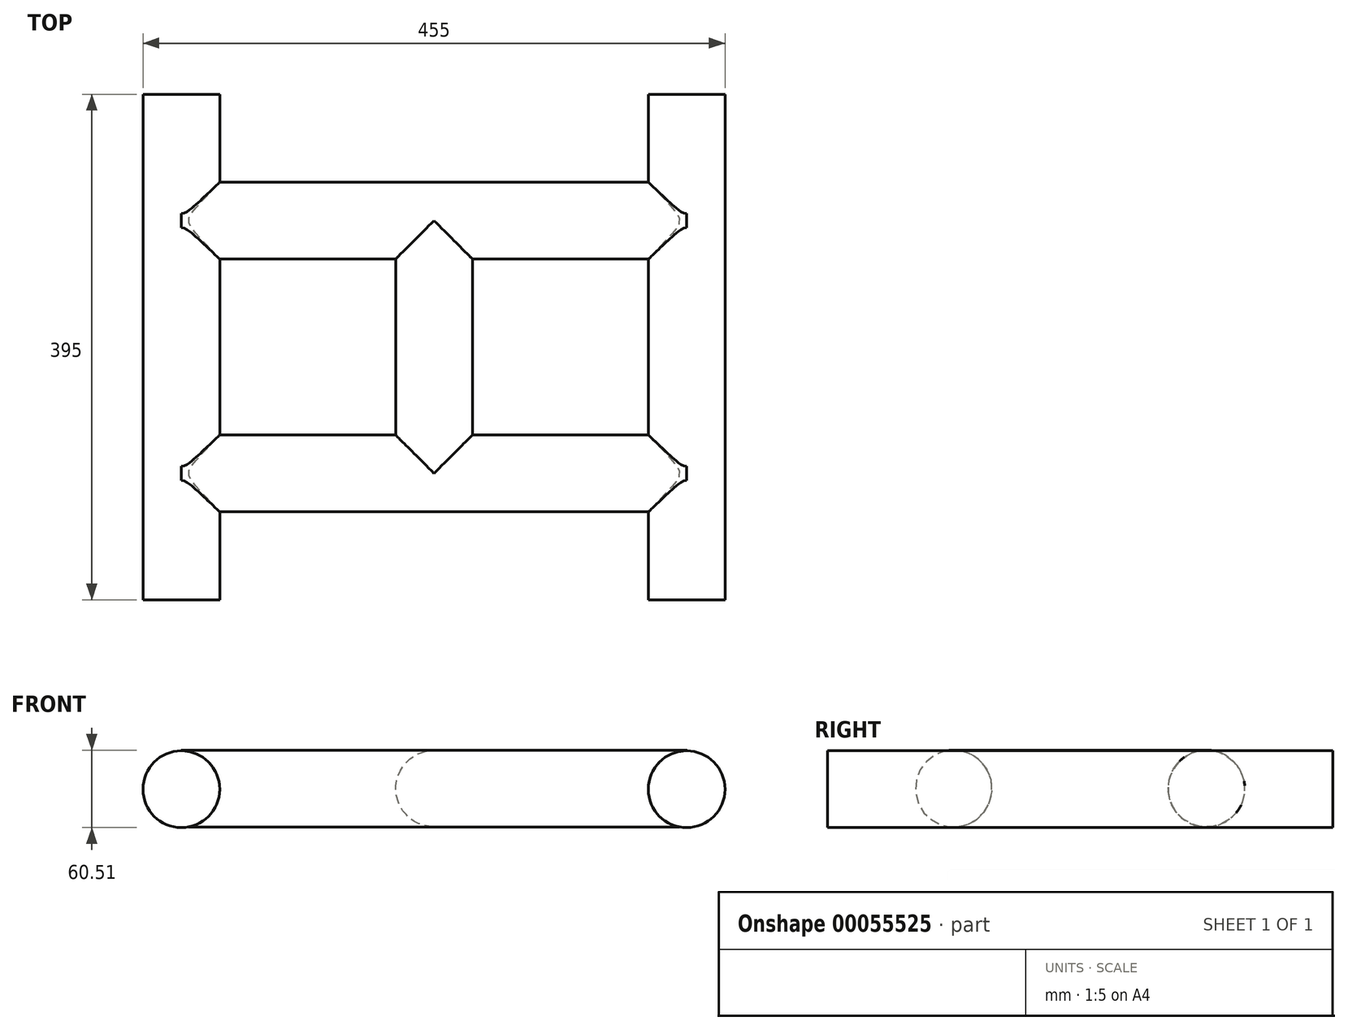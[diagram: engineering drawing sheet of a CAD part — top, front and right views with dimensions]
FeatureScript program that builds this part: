
annotation { "Feature Type Name" : "Feature", "Feature Type Description" : "" }
export const myFeature = defineFeature(function(context is Context, id is Id, definition is map)
    precondition{}
    {
        {
            var Q0;
            Q0=qCreatedBy(makeId("Front.planeOp"),FACE);
            var sketch = newSketch(context, id + "F0", { "sketchPlane" : qUnion([Q0])});
            skCircle(sketch, "E0", {"center": v(0, 0) * mm, "radius": 30 * mm});
            skCircle(sketch, "E1", {"center": v(-197.5, -0.5) * mm, "radius": 30 * mm});
            skSolve(sketch);
        }
        {
            var Q0;
            Q0=makeQuery(id+"F0.imprint","IMPRINT",FACE,{"disambiguationData":[TD([[makeQuery(id+"F0.imprint","IMPRINT",EDGE,{"derivedFrom":sQuery(id+"F0.wireOp",EDGE,"E1")}),1.0]])]});
            extrude(context, id + "F1", {"entities" : qUnion([Q0]), "endBound" : BoundingType.SYMMETRIC, "depth" : 395 * mm});
        }
        {
            var Q0;
            Q0 = qSketchRegion(id + "F0", true);
            extrude(context, id + "F2", {"entities" : qUnion([Q0]), "operationType" : NewBodyOperationType.ADD, "endBound" : BoundingType.SYMMETRIC, "depth" : 395 / 2 * mm});
        }
        {
            var Q0;
            Q0=makeQuery(id+"F2.opExtrude","SWEPT_BODY",BODY,{"disambiguationData":[OSD([sQuery(id+"F0.wireOp",EDGE,"E0")])]});
            var Q1;
            Q1=makeQuery(id+"F1.opExtrude","SWEPT_BODY",BODY,{"disambiguationData":[OSD([sQuery(id+"F0.wireOp",EDGE,"E1")])]});
            var Q2;
            Q2=qCreatedBy(makeId("Right.planeOp"),FACE);
            mirror(context, id + "F3", {"operationType" : NewBodyOperationType.ADD, "entities" : qUnion([Q0, Q1]), "mirrorPlane" : qUnion([Q2])});
        }
        {
            var Q0;
            Q0=qCreatedBy(makeId("Right.planeOp"),FACE);
            var sketch = newSketch(context, id + "F4", { "sketchPlane" : qUnion([Q0])});
            skCircle(sketch, "E2", {"center": v(98.75, 0) * mm, "radius": 30 * mm});
            skCircle(sketch, "E3", {"center": v(-98.75, 0) * mm, "radius": 30 * mm});
            skSolve(sketch);
        }
        {
            var Q0;
            Q0=makeQuery(id+"F4.imprint","IMPRINT",FACE,{"disambiguationData":[TD([[makeQuery(id+"F4.imprint","IMPRINT",EDGE,{"derivedFrom":sQuery(id+"F4.wireOp",EDGE,"E3")}),1.0]])]});
            var Q1;
            Q1=makeQuery(id+"F4.imprint","IMPRINT",FACE,{"disambiguationData":[TD([[makeQuery(id+"F4.imprint","IMPRINT",EDGE,{"derivedFrom":sQuery(id+"F4.wireOp",EDGE,"E2")}),1.0]])]});
            extrude(context, id + "F5", {"entities" : qUnion([Q0, Q1]), "operationType" : NewBodyOperationType.ADD, "endBound" : BoundingType.SYMMETRIC, "depth" : 395 * mm});
        }
    });
